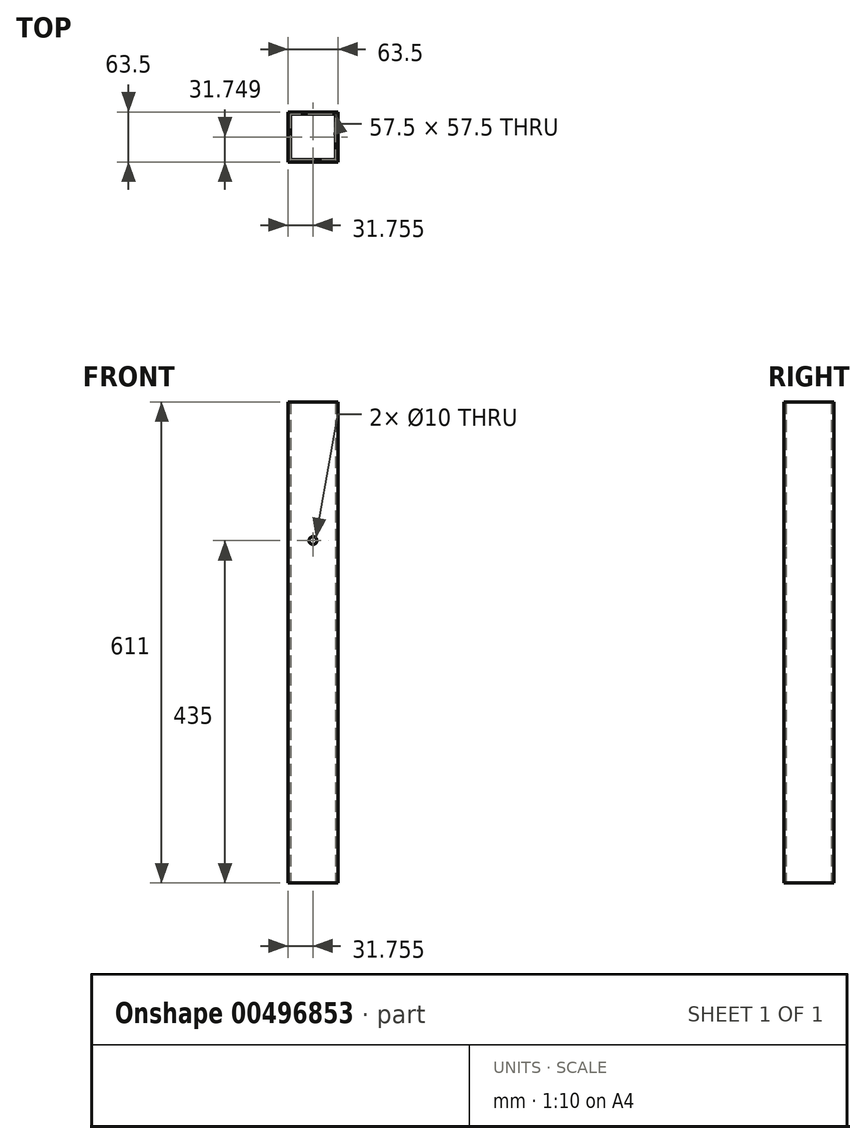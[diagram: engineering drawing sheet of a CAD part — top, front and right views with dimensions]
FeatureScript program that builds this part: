
annotation { "Feature Type Name" : "Feature", "Feature Type Description" : "" }
export const myFeature = defineFeature(function(context is Context, id is Id, definition is map)
    precondition{}
    {
        {
            var Q0;
            Q0=qCreatedBy(makeId("Top.planeOp"),FACE);
            var sketch = newSketch(context, id + "F0", { "sketchPlane" : qUnion([Q0])});
            skLineSegment(sketch, "E0.bottom", {"start": v(-23.17, 28.15) * mm, "end": v(34.33, 28.15) * mm});
            skLineSegment(sketch, "E0.top", {"start": v(-23.17, -29.35) * mm, "end": v(34.33, -29.35) * mm});
            skLineSegment(sketch, "E0.left", {"start": v(-23.17, 28.15) * mm, "end": v(-23.17, -29.35) * mm});
            skLineSegment(sketch, "E0.right", {"start": v(34.33, 28.15) * mm, "end": v(34.33, -29.35) * mm});
            skLineSegment(sketch, "E1.bottom", {"start": v(-26.17, 31.15) * mm, "end": v(37.33, 31.15) * mm});
            skLineSegment(sketch, "E1.top", {"start": v(-26.17, -32.35) * mm, "end": v(37.33, -32.35) * mm});
            skLineSegment(sketch, "E1.left", {"start": v(-26.17, 31.15) * mm, "end": v(-26.17, -32.35) * mm});
            skLineSegment(sketch, "E1.right", {"start": v(37.33, 31.15) * mm, "end": v(37.33, -32.35) * mm});
            skSolve(sketch);
        }
        {
            var Q0;
            Q0=qSketchRegion(id+"F0",true);
            extrude(context, id + "F1", {"entities" : qUnion([Q0]), "flatOperationType" : FlatOperationType.REMOVE, "offsetDistance" : 25 * mm, "depth" : 611 * mm, "domain" : OperationDomain.MODEL});
        }
        {
            var Q0;
            Q0=makeQuery(id+"F1.opExtrude","SWEPT_FACE",FACE,{"disambiguationData":[OSD([sQuery(id+"F0.wireOp",EDGE,"E1.bottom")])]});
            var sketch = newSketch(context, id + "F2", { "sketchPlane" : qUnion([Q0])});
            skCircle(sketch, "E2", {"center": v(-5.58, 435) * mm, "radius": 5 * mm});
            skSolve(sketch);
        }
        {
            var Q0;
            Q0 = qSketchRegion(id + "F2", true);
            extrude(context, id + "F3", {"entities" : qUnion([Q0]), "operationType" : NewBodyOperationType.REMOVE, "oppositeDirection" : true, "depth" : 70 * mm, "offsetDistance" : 25 * mm});
        }
    });
